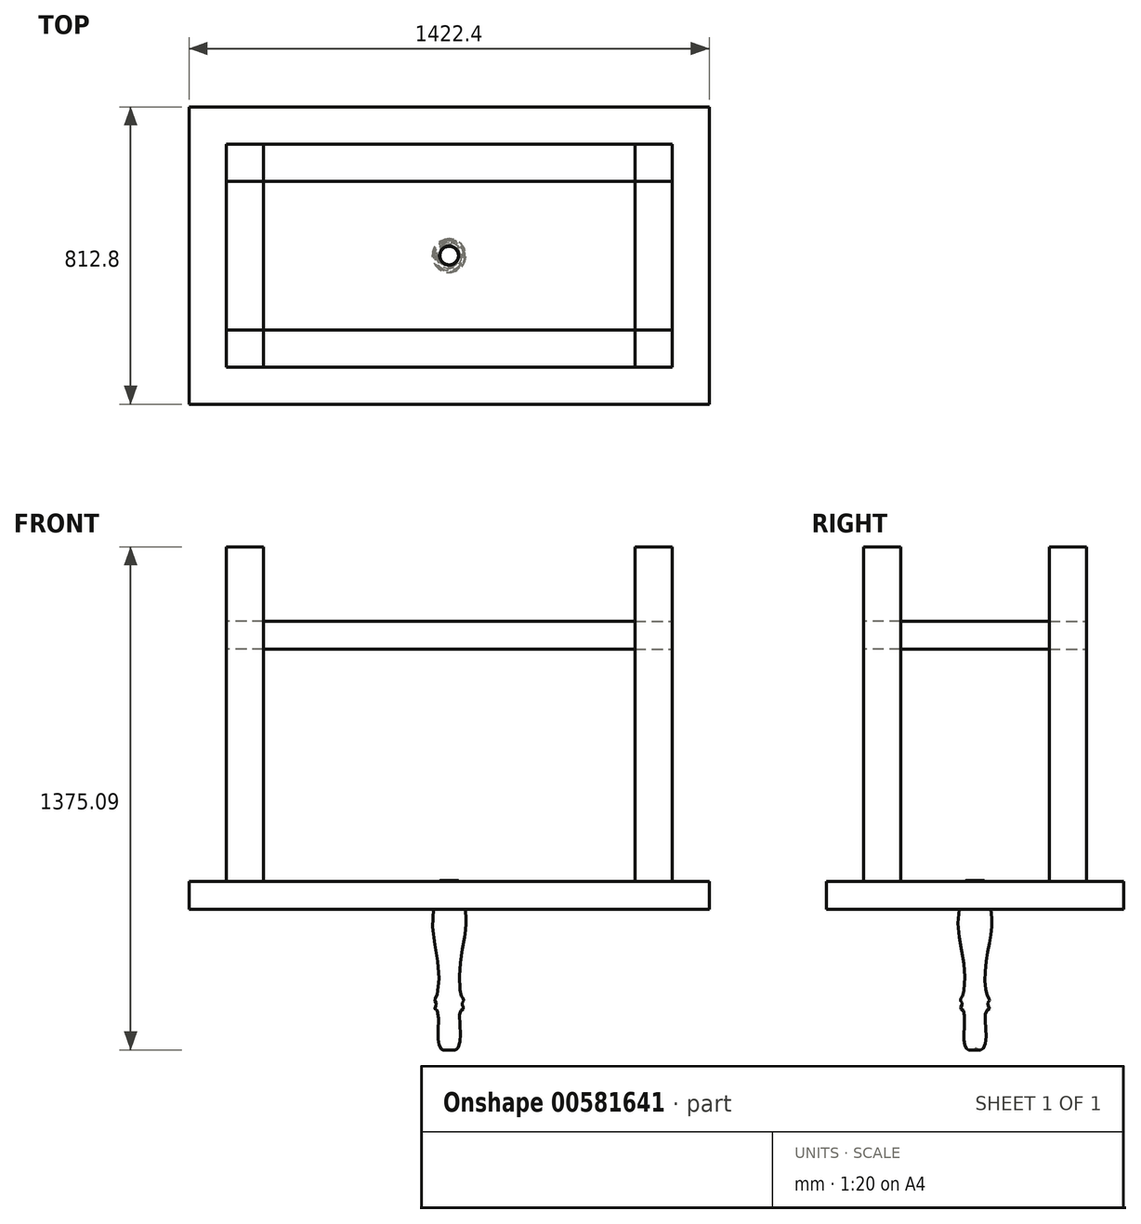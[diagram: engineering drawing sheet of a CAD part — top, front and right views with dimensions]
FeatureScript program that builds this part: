
annotation { "Feature Type Name" : "Feature", "Feature Type Description" : "" }
export const myFeature = defineFeature(function(context is Context, id is Id, definition is map)
    precondition{}
    {
        {
            var Q0;
            Q0=qCreatedBy(makeId("Top.planeOp"),FACE);
            var sketch = newSketch(context, id + "F0", { "sketchPlane" : qUnion([Q0])});
            skLineSegment(sketch, "E0.left", {"start": v(-21.35, 0) * mm, "end": v(-21.35, 0) * mm});
            skLineSegment(sketch, "E0.right", {"start": v(21.35, 0) * mm, "end": v(21.35, 0) * mm});
            skLineSegment(sketch, "E1.bottom", {"start": v(-609.6, 304.8) * mm, "end": v(-508, 304.8) * mm});
            skLineSegment(sketch, "E1.top", {"start": v(-609.6, -304.8) * mm, "end": v(-508, -304.8) * mm});
            skLineSegment(sketch, "E1.left", {"start": v(-609.6, 304.8) * mm, "end": v(-609.6, 203.2) * mm});
            skLineSegment(sketch, "E1.right", {"start": v(609.6, 304.8) * mm, "end": v(609.6, 203.2) * mm});
            skPoint(sketch, "E1.middle", {"position": v(0, 0) * mm});
            skLineSegment(sketch, "E2.bottom", {"start": v(609.6, 304.8) * mm, "end": v(508, 304.8) * mm});
            skLineSegment(sketch, "E2.top", {"start": v(609.6, 203.2) * mm, "end": v(508, 203.2) * mm});
            skLineSegment(sketch, "E2.right", {"start": v(508, 304.8) * mm, "end": v(508, 203.2) * mm});
            skLineSegment(sketch, "E3.bottom", {"start": v(609.6, -304.8) * mm, "end": v(508, -304.8) * mm});
            skLineSegment(sketch, "E3.top", {"start": v(609.6, -203.2) * mm, "end": v(508, -203.2) * mm});
            skLineSegment(sketch, "E3.left", {"start": v(609.6, -304.8) * mm, "end": v(609.6, -203.2) * mm});
            skLineSegment(sketch, "E3.right", {"start": v(508, -304.8) * mm, "end": v(508, -203.2) * mm});
            skLineSegment(sketch, "E4.top", {"start": v(-609.6, -203.2) * mm, "end": v(-508, -203.2) * mm});
            skLineSegment(sketch, "E4.left", {"start": v(-609.6, -304.8) * mm, "end": v(-609.6, -203.2) * mm});
            skLineSegment(sketch, "E4.right", {"start": v(-508, -304.8) * mm, "end": v(-508, -203.2) * mm});
            skLineSegment(sketch, "E5.top", {"start": v(-609.6, 203.2) * mm, "end": v(-508, 203.2) * mm});
            skLineSegment(sketch, "E5.right", {"start": v(-508, 304.8) * mm, "end": v(-508, 203.2) * mm});
            skLineSegment(sketch, "E6.trimOffspring", {"start": v(508, 304.8) * mm, "end": v(609.6, 304.8) * mm});
            skLineSegment(sketch, "E7.trimOffspring", {"start": v(609.6, -203.2) * mm, "end": v(609.6, -304.8) * mm});
            skLineSegment(sketch, "E8.trimOffspring", {"start": v(508, -304.8) * mm, "end": v(609.6, -304.8) * mm});
            skLineSegment(sketch, "E9.trimOffspring", {"start": v(-609.6, -203.2) * mm, "end": v(-609.6, -304.8) * mm});
            skSolve(sketch);
        }
        {
            var Q0;
            Q0 = qSketchRegion(id + "F0", true);
            extrude(context, id + "F1", {"entities" : qUnion([Q0]), "depth" : 914.4 * mm, "offsetDistance" : 25.4 * mm});
        }
        {
            var Q0;
            Q0=makeQuery(id+"F1.opExtrude","SWEPT_FACE",FACE,{"disambiguationData":[OSD([sQuery(id+"F0.wireOp",EDGE,"E4.right")])]});
            var sketch = newSketch(context, id + "F2", { "sketchPlane" : qUnion([Q0])});
            skLineSegment(sketch, "E10.bottom", {"start": v(-203.2, 635) * mm, "end": v(-304.8, 635) * mm});
            skLineSegment(sketch, "E10.top", {"start": v(-203.2, 711.2) * mm, "end": v(-304.8, 711.2) * mm});
            skLineSegment(sketch, "E10.left", {"start": v(-203.2, 635) * mm, "end": v(-203.2, 711.2) * mm});
            skLineSegment(sketch, "E10.right", {"start": v(-304.8, 635) * mm, "end": v(-304.8, 711.2) * mm});
            skLineSegment(sketch, "E11", {"start": v(0, 0) * mm, "end": v(0, 1088.3) * mm});
            skLineSegment(sketch, "E12.MirrorCS", {"start": v(203.2, 711.2) * mm, "end": v(304.8, 711.2) * mm});
            skLineSegment(sketch, "E13.MirrorCS", {"start": v(203.2, 635) * mm, "end": v(203.2, 711.2) * mm});
            skLineSegment(sketch, "E14.MirrorCS", {"start": v(203.2, 635) * mm, "end": v(304.8, 635) * mm});
            skLineSegment(sketch, "E15.MirrorCS", {"start": v(304.8, 635) * mm, "end": v(304.8, 711.2) * mm});
            skSolve(sketch);
        }
        {
            var Q0;
            Q0 = qSketchRegion(id + "F2", true);
            extrude(context, id + "F3", {"entities" : qUnion([Q0]), "depth" : 1016 * mm, "offsetDistance" : 25.4 * mm});
        }
        {
            var Q0;
            Q0=makeQuery(id+"F1.opExtrude","SWEPT_FACE",FACE,{"disambiguationData":[OSD([sQuery(id+"F0.wireOp",EDGE,"E3.top")])]});
            var sketch = newSketch(context, id + "F4", { "sketchPlane" : qUnion([Q0])});
            skLineSegment(sketch, "E16", {"start": v(-508, 711.2) * mm, "end": v(-609.6, 711.2) * mm});
            skLineSegment(sketch, "E17", {"start": v(-508, 635) * mm, "end": v(-609.6, 635) * mm});
            skLineSegment(sketch, "E18", {"start": v(508, 635) * mm, "end": v(609.6, 635) * mm});
            skLineSegment(sketch, "E19", {"start": v(508, 711.2) * mm, "end": v(609.6, 711.2) * mm});
            skLineSegment(sketch, "E20", {"start": v(609.6, 635) * mm, "end": v(609.6, 711.2) * mm});
            skLineSegment(sketch, "E21", {"start": v(508, 711.2) * mm, "end": v(508, 635) * mm});
            skLineSegment(sketch, "E22", {"start": v(-508, 711.2) * mm, "end": v(-508, 635) * mm});
            skLineSegment(sketch, "E23", {"start": v(-609.6, 635) * mm, "end": v(-609.6, 711.2) * mm});
            skSolve(sketch);
        }
        {
            var Q0;
            Q0 = qSketchRegion(id + "F4", true);
            extrude(context, id + "F5", {"entities" : qUnion([Q0]), "depth" : 406.4 * mm, "offsetDistance" : 25.4 * mm});
        }
        {
            var Q0;
            Q0=qCreatedBy(makeId("Front.planeOp"),FACE);
            var sketch = newSketch(context, id + "F6", { "sketchPlane" : qUnion([Q0])});
            skLineSegment(sketch, "E24.bottom", {"start": v(-711.2, 0) * mm, "end": v(711.2, 0) * mm});
            skLineSegment(sketch, "E24.top", {"start": v(-711.2, -76.2) * mm, "end": v(711.2, -76.2) * mm});
            skLineSegment(sketch, "E24.left", {"start": v(-711.2, 0) * mm, "end": v(-711.2, -76.2) * mm});
            skLineSegment(sketch, "E24.right", {"start": v(711.2, 0) * mm, "end": v(711.2, -76.2) * mm});
            skSolve(sketch);
        }
        {
            var Q0;
            Q0 = qSketchRegion(id + "F6", true);
            extrude(context, id + "F7", {"entities" : qUnion([Q0]), "oppositeDirection" : true, "depth" : 406.4 * mm, "offsetDistance" : 25.4 * mm, "hasSecondDirection" : true, "secondDirectionOppositeDirection" : false, "secondDirectionDepth" : 406.4 * mm});
        }
        {
            var Q0;
            Q0=qCreatedBy(makeId("Right.planeOp"),FACE);
            var sketch = newSketch(context, id + "F8", { "sketchPlane" : qUnion([Q0])});
            skLineSegment(sketch, "E25", {"start": v(0, 0) * mm, "end": v(0, -454.88) * mm});
            skFitSpline(sketch, "E26", {"points": [v(25.46, 1.82) * mm, v(46.22, -109.11) * mm, v(31.33, -216.59) * mm, v(34.05, -313.8) * mm, v(40.63, -324.16) * mm, v(34.77, -335.27) * mm, v(39.78, -346.72) * mm, v(31.9, -353.88) * mm, v(30.47, -417.57) * mm, v(19.74, -459.8) * mm, v(0, -454.88) * mm], "startDerivative": vector(161.79, -658.4) * mm, "endDerivative": vector(-308.5, 161.22) * mm});
            skLineSegment(sketch, "E27", {"start": v(25.46, 1.82) * mm, "end": v(0, 0) * mm});
            skSolve(sketch);
        }
        {
            var Q0;
            Q0 = qSketchRegion(id + "F8", true);
            var Q1;
            Q1=sQuery(id+"F8.wireOp",EDGE,"E25");
            revolve(context, id + "F9", {"operationType" : NewBodyOperationType.ADD, "entities" : qUnion([Q0]), "axis" : qUnion([Q1]), "revolveType" : RevolveType.FULL});
        }
    });
